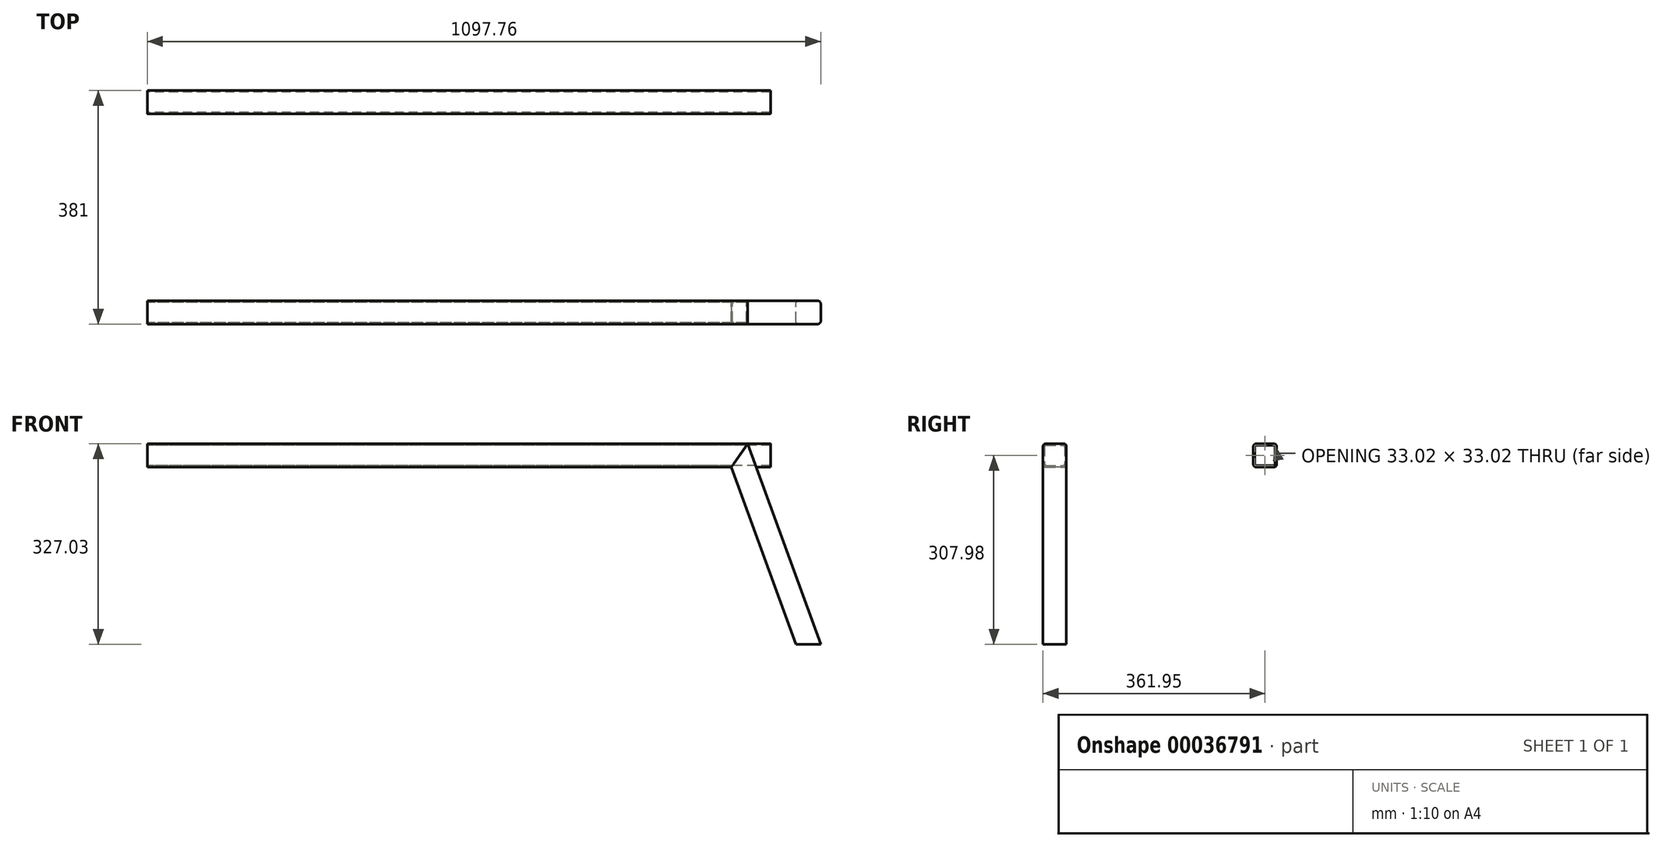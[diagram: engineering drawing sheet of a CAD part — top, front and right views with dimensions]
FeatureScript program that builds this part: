
annotation { "Feature Type Name" : "Feature", "Feature Type Description" : "" }
export const myFeature = defineFeature(function(context is Context, id is Id, definition is map)
    precondition{}
    {
        {
            var Q0;
            Q0=qCreatedBy(makeId("Right.planeOp"),FACE);
            var sketch = newSketch(context, id + "F0", { "sketchPlane" : qUnion([Q0])});
            skLineSegment(sketch, "E0.bottom", {"start": v(4.57, 0) * mm, "end": v(33.53, 0) * mm});
            skLineSegment(sketch, "E0.top", {"start": v(4.57, 38.1) * mm, "end": v(33.53, 38.1) * mm});
            skLineSegment(sketch, "E0.left", {"start": v(0, 4.57) * mm, "end": v(0, 33.53) * mm});
            skLineSegment(sketch, "E0.right", {"start": v(38.1, 4.57) * mm, "end": v(38.1, 33.53) * mm});
            skLineSegment(sketch, "E1.0", {"start": v(5.59, 35.56) * mm, "end": v(32.51, 35.56) * mm});
            skLineSegment(sketch, "E1.1", {"start": v(2.54, 5.59) * mm, "end": v(2.54, 32.51) * mm});
            skLineSegment(sketch, "E1.2", {"start": v(5.59, 2.54) * mm, "end": v(32.51, 2.54) * mm});
            skLineSegment(sketch, "E1.3", {"start": v(35.56, 5.59) * mm, "end": v(35.56, 32.51) * mm});
            skPoint(sketch, "E2.visualSharp", {"position": v(38.1, 38.1) * mm});
            skArc(sketch, "E2.filletArc", {"start": v(38.1, 33.53) * mm, "mid": v(36.76, 36.76) * mm, "end": v(33.53, 38.1) * mm});
            skPoint(sketch, "E3.visualSharp", {"position": v(38.1, 0) * mm});
            skArc(sketch, "E3.filletArc", {"start": v(33.53, 0) * mm, "mid": v(36.76, 1.34) * mm, "end": v(38.1, 4.57) * mm});
            skPoint(sketch, "E4.visualSharp", {"position": v(0, 0) * mm});
            skArc(sketch, "E4.filletArc", {"start": v(0, 4.57) * mm, "mid": v(1.34, 1.34) * mm, "end": v(4.57, 0) * mm});
            skPoint(sketch, "E5.visualSharp", {"position": v(0, 38.1) * mm});
            skArc(sketch, "E5.filletArc", {"start": v(4.57, 38.1) * mm, "mid": v(1.34, 36.76) * mm, "end": v(0, 33.53) * mm});
            skPoint(sketch, "E6.visualSharp", {"position": v(2.54, 35.56) * mm});
            skArc(sketch, "E6.filletArc", {"start": v(5.59, 35.56) * mm, "mid": v(3.43, 34.67) * mm, "end": v(2.54, 32.51) * mm});
            skPoint(sketch, "E7.visualSharp", {"position": v(2.54, 2.54) * mm});
            skArc(sketch, "E7.filletArc", {"start": v(2.54, 5.59) * mm, "mid": v(3.43, 3.43) * mm, "end": v(5.59, 2.54) * mm});
            skPoint(sketch, "E8.visualSharp", {"position": v(35.56, 2.54) * mm});
            skArc(sketch, "E8.filletArc", {"start": v(32.51, 2.54) * mm, "mid": v(34.67, 3.43) * mm, "end": v(35.56, 5.59) * mm});
            skPoint(sketch, "E9.visualSharp", {"position": v(35.56, 35.56) * mm});
            skArc(sketch, "E9.filletArc", {"start": v(35.56, 32.51) * mm, "mid": v(34.67, 34.67) * mm, "end": v(32.51, 35.56) * mm});
            skSolve(sketch);
        }
        {
            var Q0;
            Q0 = qSketchRegion(id + "F0", true);
            extrude(context, id + "F1", {"entities" : qUnion([Q0]), "depth" : 1016 * mm});
        }
        {
            var Q0;
            Q0=qCreatedBy(makeId("Front.planeOp"),FACE);
            cPlane(context, id + "F2", {"entities" : qUnion([Q0]), "cplaneType" : CPlaneType.OFFSET, "offset" : 152.4 * mm, "width" : 152.4 * mm, "height" : 152.4 * mm});
        }
        {
            var Q0;
            Q0=makeQuery(id+"F1.opExtrude","SWEPT_BODY",BODY,{"disambiguationData":[OSD([sQuery(id+"F0.wireOp",EDGE,"E0.bottom"),sQuery(id+"F0.wireOp",EDGE,"E0.top"),sQuery(id+"F0.wireOp",EDGE,"E0.left"),sQuery(id+"F0.wireOp",EDGE,"E0.right"),sQuery(id+"F0.wireOp",EDGE,"E1.0"),sQuery(id+"F0.wireOp",EDGE,"E1.1"),sQuery(id+"F0.wireOp",EDGE,"E1.2"),sQuery(id+"F0.wireOp",EDGE,"E1.3"),sQuery(id+"F0.wireOp",EDGE,"E2.filletArc"),sQuery(id+"F0.wireOp",EDGE,"E3.filletArc"),sQuery(id+"F0.wireOp",EDGE,"E4.filletArc"),sQuery(id+"F0.wireOp",EDGE,"E5.filletArc"),sQuery(id+"F0.wireOp",EDGE,"E6.filletArc"),sQuery(id+"F0.wireOp",EDGE,"E7.filletArc"),sQuery(id+"F0.wireOp",EDGE,"E8.filletArc"),sQuery(id+"F0.wireOp",EDGE,"E9.filletArc")])]});
            var Q1;
            Q1=qCreatedBy(id+"F2.planeOp",FACE);
            mirror(context, id + "F3", {"entities" : qUnion([Q0]), "mirrorPlane" : qUnion([Q1])});
        }
        {
            var Q0;
            Q0=makeQuery(id+"F3.opPattern","COPY",FACE,{"derivedFrom":makeQuery(id+"F1.opExtrude","SWEPT_FACE",FACE,{"disambiguationData":[OSD([sQuery(id+"F0.wireOp",EDGE,"E0.right")])]}),"instanceName":"1"});
            var sketch = newSketch(context, id + "F4", { "sketchPlane" : qUnion([Q0])});
            skLineSegment(sketch, "E10.0", {"start": v(1016, 0) * mm, "end": v(0, 0) * mm});
            skLineSegment(sketch, "E11", {"start": v(1016, 0) * mm, "end": v(1018.38, 0) * mm});
            skLineSegment(sketch, "E12", {"start": v(1018.38, 0) * mm, "end": v(1018.38, -288.93) * mm});
            skLineSegment(sketch, "E13", {"start": v(1018.38, -288.93) * mm, "end": v(1097.76, -288.93) * mm});
            skLineSegment(sketch, "E14", {"start": v(1097.76, -288.93) * mm, "end": v(914.47, 214.64) * mm});
            skSolve(sketch);
        }
        {
            var Q0;
            Q0=makeQuery(id+"F1.opExtrude","CAP_VERTEX",VERTEX,{"disambiguationData":[OSD([sQuery(id+"F0.wireOp",EDGE,"E0.bottom"),sQuery(id+"F0.wireOp",EDGE,"E4.filletArc")])],"isStart":false});
            var Q1;
            Q1=makeQuery(id+"F1.opExtrude","CAP_VERTEX",VERTEX,{"disambiguationData":[OSD([sQuery(id+"F0.wireOp",EDGE,"E0.left"),sQuery(id+"F0.wireOp",EDGE,"E4.filletArc")])],"isStart":false});
            var Q2;
            Q2=makeQuery(id+"F1.opExtrude","CAP_VERTEX",VERTEX,{"disambiguationData":[OSD([sQuery(id+"F0.wireOp",EDGE,"E0.left"),sQuery(id+"F0.wireOp",EDGE,"E4.filletArc")])],"isStart":true});
            cPlane(context, id + "F5", {"entities" : qUnion([Q0, Q1, Q2]), "cplaneType" : CPlaneType.THREE_POINT, "offset" : 152.4 * mm, "width" : 152.4 * mm, "height" : 152.4 * mm});
        }
        {
            var Q0;
            Q0=qCreatedBy(id+"F5.planeOp",FACE);
            var sketch = newSketch(context, id + "F6", { "sketchPlane" : qUnion([Q0])});
            skLineSegment(sketch, "E15.0", {"start": v(1016, 3.23) * mm, "end": v(1016, -3.23) * mm});
            skLineSegment(sketch, "E16.0", {"start": v(0, 3.23) * mm, "end": v(0, -3.23) * mm});
            skCircle(sketch, "E17", {"center": v(914.4, 0) * mm, "radius": 2.38 * mm});
            skCircle(sketch, "E18", {"center": v(101.6, 0) * mm, "radius": 2.38 * mm});
            skSolve(sketch);
        }
        {
            var Q0;
            Q0 = qSketchRegion(id + "F6", true);
            extrude(context, id + "F7", {"entities" : qUnion([Q0]), "operationType" : NewBodyOperationType.REMOVE, "oppositeDirection" : true, "depth" : 25.4 * mm, "hasSecondDirection" : true, "secondDirectionOppositeDirection" : false, "secondDirectionDepth" : 25.4 * mm});
        }
        {
            var Q0;
            {var subQ1=sQuery(id+"F0.wireOp",EDGE,"E0.right");var subQ6=makeQuery(id+"F3.opPattern","COPY",EDGE,{"derivedFrom":makeQuery(id+"F1.opExtrude","CAP_EDGE",EDGE,{"disambiguationData":[OSD([subQ1])],"isStart":true}),"instanceName":"1"});Q0=makeQuery(id+"F4.imprint","IMPRINT",FACE,{"disambiguationData":[TD([[makeQuery(id+"F4.imprint","IMPRINT",EDGE,{"derivedFrom":subQ6}),-1.0]])]});}
            var sketch = newSketch(context, id + "F8", { "sketchPlane" : qUnion([Q0])});
            skLineSegment(sketch, "E19.0", {"start": v(1097.76, -288.93) * mm, "end": v(997.05, -12.25) * mm});
            skLineSegment(sketch, "E20.0", {"start": v(1061.95, -301.96) * mm, "end": v(957.49, -14.94) * mm});
            skLineSegment(sketch, "E21.0", {"start": v(1016, 38.1) * mm, "end": v(0, 38.1) * mm});
            skLineSegment(sketch, "E22.0", {"start": v(952.05, 0) * mm, "end": v(0, 0) * mm});
            skLineSegment(sketch, "E23", {"start": v(952.05, 0) * mm, "end": v(978.73, 38.1) * mm});
            skPoint(sketch, "E24.orphan", {"position": v(914.47, 214.64) * mm});
            skLineSegment(sketch, "E25", {"start": v(978.73, 38.1) * mm, "end": v(1012.42, 54.09) * mm});
            skLineSegment(sketch, "E26", {"start": v(1012.42, 54.09) * mm, "end": v(1040.92, 51.43) * mm});
            skLineSegment(sketch, "E27", {"start": v(1040.92, 51.43) * mm, "end": v(1035.24, -9.65) * mm});
            skLineSegment(sketch, "E28", {"start": v(1035.24, -9.65) * mm, "end": v(947.5, -15.62) * mm});
            skLineSegment(sketch, "E29", {"start": v(947.5, -15.62) * mm, "end": v(952.05, 0) * mm});
            skPoint(sketch, "E30.orphan", {"position": v(1016, 0) * mm});
            skSolve(sketch);
        }
        {
            var Q0;
            Q0 = qSketchRegion(id + "F8", true);
            extrude(context, id + "F9", {"entities" : qUnion([Q0]), "operationType" : NewBodyOperationType.REMOVE, "oppositeDirection" : true, "depth" : 50.8 * mm});
        }
        {
            var Q0;
            Q0 = qSketchRegion(id + "F8", true);
            extrude(context, id + "F10", {"entities" : qUnion([Q0]), "operationType" : NewBodyOperationType.REMOVE, "oppositeDirection" : true, "depth" : 50.8 * mm});
        }
        {
            var Q0;
            Q0=sQuery(id+"F4.wireOp",VERTEX,"E13.end");
            var Q1;
            Q1=sQuery(id+"F4.wireOp",EDGE,"E14");
            cPlane(context, id + "F11", {"entities" : qUnion([Q0, Q1]), "cplaneType" : CPlaneType.LINE_POINT, "offset" : 152.4 * mm, "width" : 152.4 * mm, "height" : 152.4 * mm});
        }
        {
            var Q0;
            Q0=qCreatedBy(id+"F11.planeOp",FACE);
            var sketch = newSketch(context, id + "F12", { "sketchPlane" : qUnion([Q0])});
            skPoint(sketch, "E31.0", {"position": v(932.74, -342.9) * mm});
            skLineSegment(sketch, "E32", {"start": v(932.74, -337.82) * mm, "end": v(932.74, -309.88) * mm});
            skLineSegment(sketch, "E33", {"start": v(927.66, -304.8) * mm, "end": v(899.72, -304.8) * mm});
            skLineSegment(sketch, "E34", {"start": v(894.64, -309.88) * mm, "end": v(894.64, -337.82) * mm});
            skLineSegment(sketch, "E35", {"start": v(899.72, -342.9) * mm, "end": v(927.66, -342.9) * mm});
            skArc(sketch, "E36.filletArc", {"start": v(927.66, -342.9) * mm, "mid": v(931.25, -341.41) * mm, "end": v(932.74, -337.82) * mm});
            skPoint(sketch, "E37.visualSharp", {"position": v(932.74, -304.8) * mm});
            skArc(sketch, "E37.filletArc", {"start": v(932.74, -309.88) * mm, "mid": v(931.25, -306.29) * mm, "end": v(927.66, -304.8) * mm});
            skPoint(sketch, "E38.visualSharp", {"position": v(894.64, -304.8) * mm});
            skArc(sketch, "E38.filletArc", {"start": v(899.72, -304.8) * mm, "mid": v(896.12, -306.29) * mm, "end": v(894.64, -309.88) * mm});
            skPoint(sketch, "E39.visualSharp", {"position": v(894.64, -342.9) * mm});
            skArc(sketch, "E39.filletArc", {"start": v(894.64, -337.82) * mm, "mid": v(896.12, -341.41) * mm, "end": v(899.72, -342.9) * mm});
            skLineSegment(sketch, "E40.0", {"start": v(899.2, -304.8) * mm, "end": v(1.56, -304.8) * mm});
            skSolve(sketch);
        }
        {
            var Q0;
            Q0 = qSketchRegion(id + "F12", true);
            var Q1;
            Q1=makeQuery(id+"F9.boolean.opBoolean","COPY",FACE,{"derivedFrom":makeQuery(id+"F9.opExtrude","SWEPT_FACE",FACE,{"disambiguationData":[OSD([sQuery(id+"F8.wireOp",EDGE,"E23")])]})});
            extrude(context, id + "F13", {"entities" : qUnion([Q0]), "endBound" : BoundingType.UP_TO_SURFACE, "endBoundEntityFace" : qUnion([Q1]), "depth" : 25.4 * mm});
        }
        {
            var Q0;
            Q0=makeQuery(id+"F13.opExtrude","SWEPT_FACE",FACE,{"disambiguationData":[OSD([sQuery(id+"F12.wireOp",EDGE,"E35")])]});
            var sketch = newSketch(context, id + "F14", { "sketchPlane" : qUnion([Q0])});
            skLineSegment(sketch, "E41", {"start": v(1018.38, -288.93) * mm, "end": v(1040.63, -307.84) * mm});
            skLineSegment(sketch, "E42", {"start": v(1040.63, -307.84) * mm, "end": v(1091.4, -315.7) * mm});
            skLineSegment(sketch, "E43", {"start": v(1091.4, -315.7) * mm, "end": v(1097.76, -288.93) * mm});
            skLineSegment(sketch, "E44", {"start": v(1018.38, -288.93) * mm, "end": v(1097.76, -288.93) * mm});
            skSolve(sketch);
        }
        {
            var Q0;
            Q0 = qSketchRegion(id + "F14", true);
            extrude(context, id + "F15", {"entities" : qUnion([Q0]), "operationType" : NewBodyOperationType.REMOVE, "oppositeDirection" : true, "depth" : 50.8 * mm});
        }
    });
